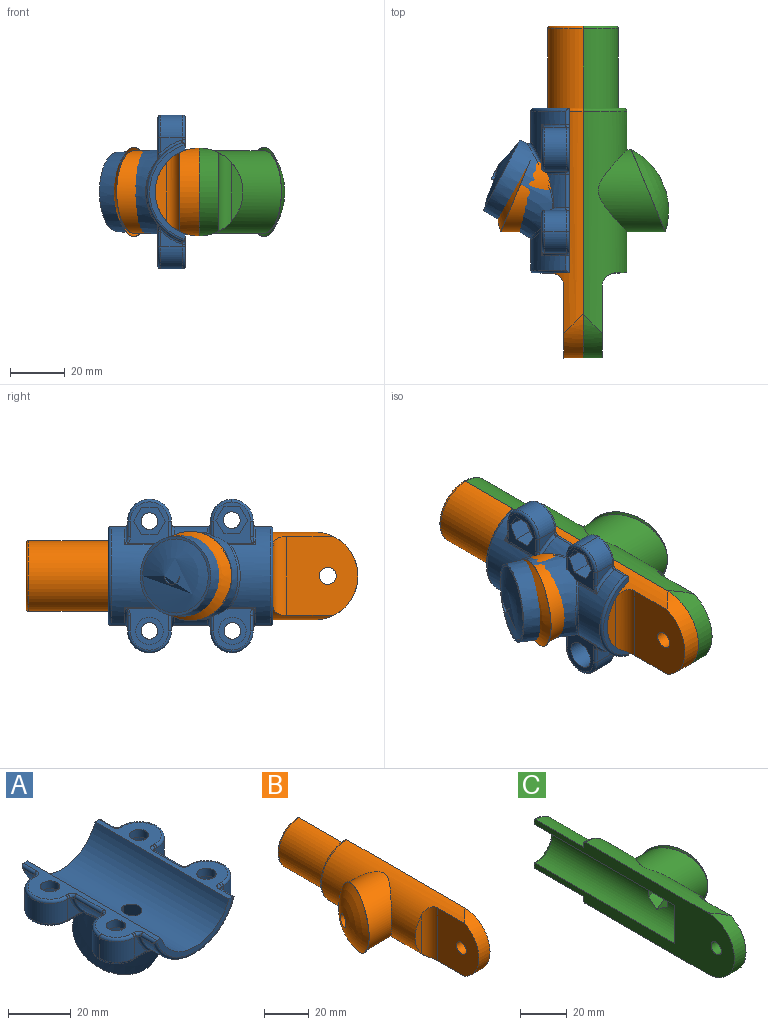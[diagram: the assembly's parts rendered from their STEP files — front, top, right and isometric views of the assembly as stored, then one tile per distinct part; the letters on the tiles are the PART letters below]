
ASSEMBLY  parts=3 mates=5
PART A: 121 faces, bbox 57.4x60.1x33.5 mm
  f0: cylinder r=19mm len=35.83mm, axis (0,1,0), area 440.5mm2, adj f56,f57,f60,f63,f65,f66,f68,f69
  f1: cylinder r=16mm len=60mm, axis (0,1,0), area 2372.6mm2, adj f7,f8,f9,f10,f51
  f2: cylinder r=19mm len=12.23mm, axis (0,1,0), area 72.3mm2, adj f53,f57,f61,f62
  f3: cylinder r=19mm len=35.83mm, axis (0,1,0), area 412.1mm2, adj f74,f77,f81,f82,f84,f85,f88,f89
  f4: cylinder r=19mm len=12.23mm, axis (0,1,0), area 72.3mm2, adj f57,f80,f86,f87
  f5: plane 15.21x15.02mm, normal (0,0,-1), area 103.2mm2, adj f37,f38,f39,f40,f41,f42,f57,f60
  f6: plane 15.1x14.4mm, normal (0,0,-1), area 88.8mm2, adj f43,f44,f45,f46,f47,f48,f49,f77
  f7: plane 60x11.8mm, normal (0,0,1), area 285.7mm2, adj f1,f9,f10,f27,f32,f68,f71,f73
  f8: plane 60x11.8mm, normal (0,0,1), area 285.7mm2, adj f1,f9,f10,f30,f35,f52,f54,f55
  f9: plane 34.56x13mm, normal (0,1,0), area 86.5mm2, adj f1,f7,f8,f63,f65,f68
  f10: plane 34.56x13mm, normal (0,-1,0), area 86.5mm2, adj f1,f7,f8,f82,f85,f89
  f11: cylinder r=8mm len=16mm, axis (0,0,1), area 201.1mm2, adj f12,f13,f52,f98
  f12: plane 8x5.72mm, normal (0,1,0), area 23.1mm2, adj f11,f55,f56,f99
  f13: plane 8x5.72mm, normal (0,-1,0), area 23.1mm2, adj f11,f53,f54,f97
  f14: plane 8x5.72mm, normal (0,-1,0), area 23.1mm2, adj f17,f79,f80,f115
  f15: plane 8x5.72mm, normal (0,1,0), area 23.1mm2, adj f17,f69,f73,f117
  f16: plane 15.21x15.01mm, normal (0,0,-1), area 111.2mm2, adj f34,f57,f66,f114,f115,f116,f117,f118
  f17: cylinder r=8mm len=16mm, axis (0,0,1), area 201.1mm2, adj f14,f15,f76,f116
  f18: cylinder r=8mm len=8mm, axis (0,0,1), area 98.7mm2, adj f19,f20,f70,f103
  f19: cylinder r=8mm len=8mm, axis (0,0,1), area 98.7mm2, adj f18,f21,f72,f104
  f20: plane 8x5.04mm, normal (0,1,0), area 22.8mm2, adj f18,f49,f61,f67,f102
  f21: plane 8x5.72mm, normal (0,-1,0), area 23.1mm2, adj f19,f74,f75,f105
  f22: plane 15.11x14.4mm, normal (0,0,-1), area 96.8mm2, adj f29,f49,f81,f84,f108,f109,f110,f111
  f23: plane 8x5.72mm, normal (0,-1,0), area 23.1mm2, adj f25,f88,f93,f111
  f24: plane 8x5.04mm, normal (0,1,0), area 22.8mm2, adj f26,f49,f87,f92,f108
  f25: cylinder r=8mm len=8mm, axis (0,0,1), area 98.7mm2, adj f23,f26,f95,f110
  f26: cylinder r=8mm len=8mm, axis (0,0,1), area 98.7mm2, adj f24,f25,f94,f109
  f27: cylinder r=3.05mm len=6.1mm, axis (0,0,-1), area 57.5mm2, adj f7,f28
  f28: plane 10x10mm, normal (0,0,-1), area 49.3mm2, adj f27,f29
  f29: cylinder r=5mm len=10mm, axis (0,0,-1), area 219.9mm2, adj f22,f28
  f30: cylinder r=3.05mm len=6.1mm, axis (0,0,-1), area 57.5mm2, adj f8,f31
  f31: plane 11.55x10mm, normal (0,0,-1), area 57.4mm2, adj f30,f43,f44,f45,f46,f47,f48
  f32: cylinder r=3.05mm len=6.1mm, axis (0,0,-1), area 57.5mm2, adj f7,f33
  f33: plane 10x10mm, normal (0,0,-1), area 49.3mm2, adj f32,f34
  f34: cylinder r=5mm len=10mm, axis (0,0,-1), area 219.9mm2, adj f16,f33
  f35: cylinder r=3.05mm len=6.1mm, axis (0,0,-1), area 57.5mm2, adj f8,f36
  f36: plane 11.55x10mm, normal (0,0,-1), area 57.4mm2, adj f35,f37,f38,f39,f40,f41,f42
  f37: plane 7x5mm, normal (-0.5,-0.87,0), area 40.4mm2, adj f5,f36,f38,f42
  f38: plane 7x5.77mm, normal (-1,0,0), area 40.4mm2, adj f5,f36,f37,f39
  f39: plane 7x5mm, normal (-0.5,0.87,0), area 40.4mm2, adj f5,f36,f38,f40
  f40: plane 7x5mm, normal (0.5,0.87,0), area 40.4mm2, adj f5,f36,f39,f41
  f41: plane 7x5.77mm, normal (1,0,0), area 40.4mm2, adj f5,f36,f40,f42
  f42: plane 7x5mm, normal (0.5,-0.87,0), area 40.4mm2, adj f5,f36,f37,f41
  f43: plane 7x5mm, normal (-0.5,-0.87,0), area 40.4mm2, adj f6,f31,f44,f48
  f44: plane 7x5.77mm, normal (-1,0,0), area 40.4mm2, adj f6,f31,f43,f45
  f45: plane 7x5mm, normal (-0.5,0.87,0), area 40.4mm2, adj f6,f31,f44,f46
  f46: plane 7x5mm, normal (0.5,0.87,0), area 40.4mm2, adj f6,f31,f45,f47
  f47: plane 7x5.77mm, normal (1,0,0), area 40.4mm2, adj f6,f31,f46,f48
  f48: plane 7x5mm, normal (0.5,-0.87,0), area 40.4mm2, adj f6,f31,f43,f47
  f49: cone r=15mm half-angle=3deg, axis (0,-0.46,0.89), area 1436.5mm2, adj f6,f20,f22,f24,f50,f57,f61,f81
  f50: plane 28.95x25.68mm, normal (0,0.46,-0.89), area 85.8mm2, adj f49,f120
  f51: cylinder r=3.05mm len=17.54mm, axis (0,0.46,-0.89), area 318mm2, adj f1,f120
  f52: torus R=7mm, axis (0,0,1), area 37.7mm2, adj f8,f11,f54,f55
  f53: torus R=20mm, axis (0,1,0), area 14.8mm2, adj f2,f13,f57,f58,f96
  f54: cylinder r=1mm len=1mm, axis (1,0,0), area 1.4mm2, adj f8,f13,f52,f58
  f55: cylinder r=1mm len=1mm, axis (-1,0,0), area 1.4mm2, adj f8,f12,f52,f59
  f56: torus R=20mm, axis (0,1,0), area 16.1mm2, adj f0,f12,f59,f100,f101
  f57: bspline ~31.51x26.9mm, area 75.5mm2, adj f0,f2,f4,f5,f16,f49,f53,f60
  f58: bspline ~2.42x2.23mm, area 3.8mm2, adj f8,f53,f54,f62
  f59: bspline ~2.42x2.39mm, area 3.8mm2, adj f8,f55,f56,f63
  f60: cylinder r=1mm len=15.48mm, axis (0,1,0), area 9mm2, adj f0,f5,f57,f101
  f61: torus R=20mm, axis (0,1,0), area 10.1mm2, adj f2,f20,f49,f57,f64
  f62: cylinder r=1mm len=12.23mm, axis (0,1,0), area 23.4mm2, adj f2,f8,f58,f64
  f63: cylinder r=1mm len=6mm, axis (0,1,0), area 10.9mm2, adj f0,f8,f9,f59,f65
  f64: bspline ~2.42x2.39mm, area 3.8mm2, adj f8,f61,f62,f67
  f65: torus R=18mm, axis (0,-1,0), area 73.7mm2, adj f0,f9,f63,f68
  f66: cylinder r=1mm len=15.48mm, axis (0,1,0), area 9mm2, adj f0,f16,f57,f119
  f67: cylinder r=1mm len=1mm, axis (-1,0,0), area 1.4mm2, adj f8,f20,f64,f70
  f68: cylinder r=1mm len=6mm, axis (0,1,0), area 10.9mm2, adj f0,f7,f9,f65,f71
  f69: torus R=20mm, axis (0,1,0), area 16.1mm2, adj f0,f15,f71,f118,f119
  f70: torus R=7mm, axis (0,0,1), area 18.5mm2, adj f8,f18,f67,f72
  f71: bspline ~2.42x2.23mm, area 3.8mm2, adj f7,f68,f69,f73
  f72: torus R=7mm, axis (0,0,1), area 18.5mm2, adj f8,f19,f70,f75
  f73: cylinder r=1mm len=1mm, axis (-1,0,0), area 1.4mm2, adj f7,f15,f71,f76
  f74: torus R=20mm, axis (0,1,0), area 16.1mm2, adj f3,f21,f78,f106,f107
  f75: cylinder r=1mm len=1mm, axis (1,0,0), area 1.4mm2, adj f8,f21,f72,f78
  f76: torus R=7mm, axis (0,0,1), area 37.7mm2, adj f7,f17,f73,f79
  f77: cylinder r=1mm len=10.42mm, axis (0,1,0), area 5.9mm2, adj f3,f6,f81,f107
  f78: bspline ~2.6x2.42mm, area 3.8mm2, adj f8,f74,f75,f82
  f79: cylinder r=1mm len=1mm, axis (1,0,0), area 1.4mm2, adj f7,f14,f76,f83
  f80: torus R=20mm, axis (0,1,0), area 14.8mm2, adj f4,f14,f57,f83,f114
  f81: bspline ~25.42x5.39mm, area 24.9mm2, adj f3,f6,f22,f49,f77,f84
  f82: cylinder r=1mm len=6.23mm, axis (0,1,0), area 11.3mm2, adj f3,f8,f10,f78,f85
  f83: bspline ~2.42x2.39mm, area 3.8mm2, adj f7,f79,f80,f86
  f84: cylinder r=1mm len=10.42mm, axis (0,1,0), area 5.9mm2, adj f3,f22,f81,f113
  f85: torus R=18mm, axis (0,-1,0), area 73.7mm2, adj f3,f10,f82,f89
  f86: cylinder r=1mm len=12.23mm, axis (0,1,0), area 23.4mm2, adj f4,f7,f83,f90
  f87: torus R=20mm, axis (0,1,0), area 10.1mm2, adj f4,f24,f49,f57,f90
  f88: torus R=20mm, axis (0,1,0), area 16.1mm2, adj f3,f23,f91,f112,f113
  f89: cylinder r=1mm len=6.23mm, axis (0,1,0), area 11.3mm2, adj f3,f7,f10,f85,f91
  f90: bspline ~2.6x2.42mm, area 3.8mm2, adj f7,f86,f87,f92
  f91: bspline ~2.42x2.39mm, area 3.8mm2, adj f7,f88,f89,f93
  f92: cylinder r=1mm len=1mm, axis (-1,0,0), area 1.4mm2, adj f7,f24,f90,f94
  f93: cylinder r=1mm len=1mm, axis (1,0,0), area 1.4mm2, adj f7,f23,f91,f95
  f94: torus R=7mm, axis (0,0,1), area 18.5mm2, adj f7,f26,f92,f95
  f95: torus R=7mm, axis (0,0,1), area 18.5mm2, adj f7,f25,f93,f94
  f96: bspline ~2.33x1.35mm, area 2.2mm2, adj f5,f53,f57,f97
  f97: cylinder r=1mm len=5.72mm, axis (-1,0,0), area 9mm2, adj f5,f13,f96,f98
  f98: torus R=7mm, axis (0,0,1), area 37.7mm2, adj f5,f11,f97,f99
  f99: cylinder r=1mm len=5.72mm, axis (1,0,0), area 9mm2, adj f5,f12,f98,f100
  f100: bspline ~3.26x1.52mm, area 2.6mm2, adj f5,f56,f99,f101
  f101: bspline ~1.55x1.43mm, area 0.4mm2, adj f56,f60,f100
  f102: cylinder r=1mm len=5.5mm, axis (1,0,0), area 8.3mm2, adj f6,f20,f49,f103
  f103: torus R=7mm, axis (0,0,1), area 18.5mm2, adj f6,f18,f102,f104
  f104: torus R=7mm, axis (0,0,1), area 18.5mm2, adj f6,f19,f103,f105
  f105: cylinder r=1mm len=5.72mm, axis (-1,0,0), area 9mm2, adj f6,f21,f104,f106
  f106: bspline ~3.26x1.52mm, area 2.6mm2, adj f6,f74,f105,f107
  f107: bspline ~1.55x1.43mm, area 0.4mm2, adj f74,f77,f106
  f108: cylinder r=1mm len=5.5mm, axis (1,0,0), area 8.3mm2, adj f22,f24,f49,f109
  f109: torus R=7mm, axis (0,0,1), area 18.5mm2, adj f22,f26,f108,f110
  f110: torus R=7mm, axis (0,0,1), area 18.5mm2, adj f22,f25,f109,f111
  f111: cylinder r=1mm len=5.72mm, axis (-1,0,0), area 9mm2, adj f22,f23,f110,f112
  f112: bspline ~3.26x1.52mm, area 2.6mm2, adj f22,f88,f111,f113
  f113: bspline ~1.55x1.43mm, area 0.4mm2, adj f84,f88,f112
  f114: bspline ~2.33x1.35mm, area 2.2mm2, adj f16,f57,f80,f115
  f115: cylinder r=1mm len=5.72mm, axis (-1,0,0), area 9mm2, adj f14,f16,f114,f116
  f116: torus R=7mm, axis (0,0,1), area 37.7mm2, adj f16,f17,f115,f117
  f117: cylinder r=1mm len=5.72mm, axis (1,0,0), area 9mm2, adj f15,f16,f116,f118
  f118: bspline ~3.26x1.52mm, area 2.6mm2, adj f16,f69,f117,f119
  f119: bspline ~1.55x1.43mm, area 0.4mm2, adj f66,f69,f118
  f120: cone r=2.3mm half-angle=75deg, axis (0,-0.46,0.89), area 562.5mm2, adj f50,f51
PART B: 21 faces, bbox 31.2x121x34.6 mm
  f0: plane 6.2x5.73mm, normal (-0.92,0.38,0), area 30.2mm2, adj f1
  f1: cylinder r=3.1mm len=7.95mm, axis (0.92,-0.38,0), area 112.9mm2, adj f0,f2
  f2: sphere r=25mm, area 910.5mm2, adj f1,f3,f4
  f3: plane 30x16.24mm, normal (0.92,-0.38,0), area 31.5mm2, adj f2,f7
  f4: plane 30x16.24mm, normal (0.92,-0.38,0), area 31.5mm2, adj f2,f7
  f5: plane 21.17x4mm, normal (0,-1,0), area 58mm2, adj f6,f19
  f6: cylinder r=5mm len=28.78mm, axis (0,0,1), area 207.6mm2, adj f5,f9,f19
  f7: cylinder r=15mm len=30mm, axis (1,0,0), area 1165.5mm2, adj f3,f4,f19
  f8: cylinder r=3.1mm len=7mm, axis (-1,0,0), area 136.3mm2, adj f9,f20
  f9: plane 28.78x26mm, normal (-1,0,0), area 644.5mm2, adj f6,f8,f18,f19
  f10: plane 20x10mm, normal (0,1,0), area 157.1mm2, adj f12,f20
  f11: torus R=11mm, axis (0,1,0), area 51.1mm2, adj f12,f14,f20
  f12: cylinder r=10mm len=84mm, axis (0,1,0), area 2638.9mm2, adj f10,f11,f20
  f13: torus R=11.9mm, axis (0,1,0), area 61.9mm2, adj f14,f15,f20
  f14: plane 23.8x11.9mm, normal (0,1,0), area 32.4mm2, adj f11,f13,f20
  f15: cylinder r=12.9mm len=29mm, axis (0,-1,0), area 1175.3mm2, adj f13,f17,f20
  f16: torus R=15mm, axis (0,-1,0), area 77.2mm2, adj f17,f19,f20
  f17: plane 30x15mm, normal (0,1,0), area 92mm2, adj f15,f16,f20
  f18: cylinder r=16mm len=32mm, axis (-1,0,0), area 302mm2, adj f9,f19,f20
  f19: cylinder r=16mm len=81mm, axis (0,-1,0), area 2407.8mm2, adj f5,f6,f7,f9,f16,f18,f20
  f20: plane 121x32mm, normal (1,0,0), area 1844.7mm2, adj f8,f10,f11,f12,f13,f14,f15,f16
PART C: 29 faces, bbox 31.6x121.4x35 mm
  f0: cylinder r=3.05mm len=8.78mm, axis (0.92,0.38,0), area 133.7mm2, adj f11,f28
  f1: cylinder r=10mm len=84mm, axis (0,1,0), area 2536.4mm2, adj f17,f18,f21,f22,f23,f24,f25,f26
  f2: plane 28.78x26mm, normal (1,0,0), area 644.5mm2, adj f3,f14,f15,f16
  f3: cylinder r=16mm len=81mm, axis (0,-1,0), area 2407.1mm2, adj f2,f4,f6,f15,f16,f20,f21
  f4: cylinder r=15mm len=30mm, axis (-1,0,0), area 1164.9mm2, adj f3,f7,f8
  f5: plane 30x15mm, normal (0,1,0), area 92mm2, adj f12,f20,f21
  f6: plane 21.17x4mm, normal (0,-1,0), area 58mm2, adj f3,f16
  f7: plane 30x16.24mm, normal (-0.92,-0.38,0), area 31.5mm2, adj f4,f9
  f8: plane 30x16.24mm, normal (-0.92,-0.38,0), area 31.5mm2, adj f4,f9
  f9: sphere r=25mm, area 910.5mm2, adj f7,f8,f10
  f10: cylinder r=3.1mm len=7.95mm, axis (-0.92,-0.38,0), area 112.9mm2, adj f9,f11
  f11: plane 6.2x5.73mm, normal (0.92,0.38,0), area 1mm2, adj f0,f10
  f12: cylinder r=12.9mm len=29mm, axis (0,-1,0), area 1175.3mm2, adj f5,f19,f21
  f13: plane 23.8x11.9mm, normal (0,1,0), area 32.4mm2, adj f18,f19,f21
  f14: cylinder r=3.1mm len=7mm, axis (-1,0,0), area 136.3mm2, adj f2,f21
  f15: cylinder r=16mm len=32mm, axis (-1,0,0), area 302mm2, adj f2,f3,f21
  f16: cylinder r=5mm len=28.78mm, axis (0,0,-1), area 207.6mm2, adj f2,f3,f6
  f17: plane 20x10mm, normal (0,1,0), area 157.1mm2, adj f1,f21
  f18: torus R=11mm, axis (0,1,0), area 51.1mm2, adj f1,f13,f21
  f19: torus R=11.9mm, axis (0,1,0), area 61.9mm2, adj f12,f13,f21
  f20: torus R=15mm, axis (0,-1,0), area 77.2mm2, adj f3,f5,f21
  f21: plane 121x32mm, normal (-1,0,0), area 1844.7mm2, adj f1,f3,f5,f12,f13,f14,f15,f17
  f22: plane 11.22x9.04mm, normal (-0.18,0.44,-0.88), area 58mm2, adj f1,f23,f27,f28
  f23: plane 9.03x8.43mm, normal (0.2,-0.49,-0.85), area 45.2mm2, adj f1,f22,f24,f28
  f24: plane 6.25x6.02mm, normal (0.38,-0.92,0.03), area 33.6mm2, adj f1,f23,f25,f28
  f25: plane 9.2x8.69mm, normal (0.18,-0.44,0.88), area 46.3mm2, adj f1,f24,f26,f28
  f26: plane 11.32x8.88mm, normal (-0.2,0.49,0.85), area 58.3mm2, adj f1,f25,f27,f28
  f27: plane 9.92x6.25mm, normal (-0.38,0.92,-0.03), area 58.5mm2, adj f1,f22,f26,f28
  f28: plane 11.77x9.6mm, normal (-0.92,-0.38,0), area 60.9mm2, adj f0,f22,f23,f24,f25,f26,f27
PLACE A rot(axis=(0,1,0),90deg) t=(-24.43,-44.6,22.74)mm
PLACE B t=(-24.43,-74.6,22.74)mm
PLACE C t=(-24.43,-74.6,22.74)mm
MATE cylindrical C.f12 <-> B.f13  axis (0,-1,0) through (-24.43,-15.6,22.74)mm
MATE planar C.f5 <-> B.f17  axis (0,1,0) through (-15.53,-44.6,22.74)mm
MATE planar A.f9 <-> C.f5  axis (0,1,0) through (-37.22,-44.6,22.74)mm
MATE cylindrical C.f3 <-> A.f1  axis (0,-1,0) through (-24.43,-45.6,22.74)mm
MATE planar C.f21 <-> B.f18  axis (-1,0,0) through (-24.43,-92.11,22.74)mm
